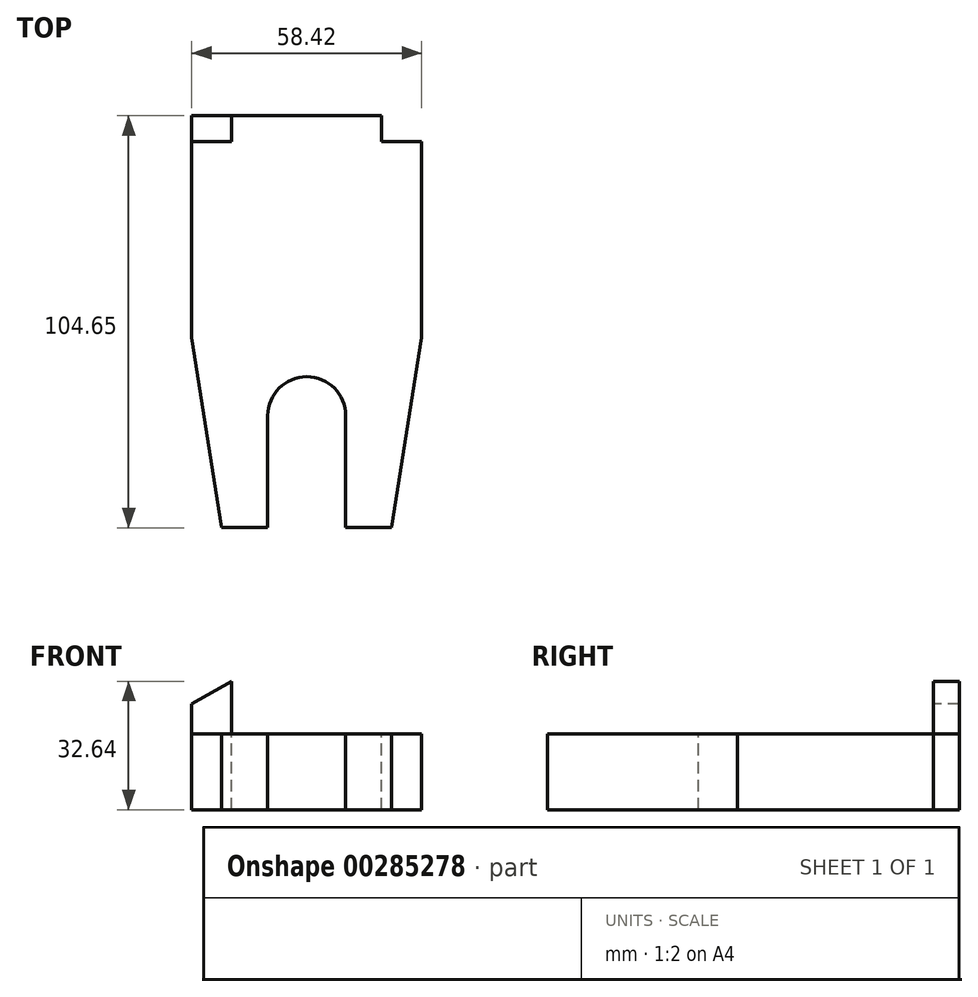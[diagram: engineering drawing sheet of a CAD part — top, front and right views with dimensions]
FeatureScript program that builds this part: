
annotation { "Feature Type Name" : "Feature", "Feature Type Description" : "" }
export const myFeature = defineFeature(function(context is Context, id is Id, definition is map)
    precondition{}
    {
        {
            var Q0;
            Q0=qCreatedBy(makeId("Front.planeOp"),FACE);
            var sketch = newSketch(context, id + "F0", { "sketchPlane" : qUnion([Q0])});
            skLineSegment(sketch, "E0.bottom", {"start": v(-54.99, -16.13) * mm, "end": v(3.43, -16.13) * mm});
            skLineSegment(sketch, "E0.top", {"start": v(-54.99, 3.18) * mm, "end": v(3.43, 3.18) * mm});
            skLineSegment(sketch, "E0.left", {"start": v(-54.99, -16.13) * mm, "end": v(-54.99, 3.18) * mm});
            skLineSegment(sketch, "E0.right", {"start": v(3.43, -16.13) * mm, "end": v(3.43, 3.18) * mm});
            skSolve(sketch);
        }
        {
            var Q0;
            Q0 = qSketchRegion(id + "F0", true);
            extrude(context, id + "F1", {"entities" : qUnion([Q0]), "depth" : 104.65 * mm});
        }
        {
            var Q0;
            Q0=makeQuery(id+"F1.opExtrude","SWEPT_FACE",FACE,{"disambiguationData":[OSD([sQuery(id+"F0.wireOp",EDGE,"E0.top")])]});
            var sketch = newSketch(context, id + "F2", { "sketchPlane" : qUnion([Q0])});
            skLineSegment(sketch, "E1", {"start": v(-25.78, -104.65) * mm, "end": v(-15.87, -104.65) * mm});
            skLineSegment(sketch, "E2", {"start": v(-25.78, -104.65) * mm, "end": v(-35.68, -104.65) * mm});
            skLineSegment(sketch, "E3", {"start": v(-15.87, -104.65) * mm, "end": v(-15.87, -76.2) * mm});
            skLineSegment(sketch, "E4", {"start": v(-15.87, -76.2) * mm, "end": v(-35.68, -76.2) * mm});
            skLineSegment(sketch, "E5", {"start": v(-35.68, -76.2) * mm, "end": v(-35.68, -104.65) * mm});
            skCircle(sketch, "E6", {"center": v(-25.78, -76.2) * mm, "radius": 9.9 * mm});
            skLineSegment(sketch, "E7", {"start": v(-54.99, -104.65) * mm, "end": v(-54.99, -56.39) * mm});
            skLineSegment(sketch, "E8", {"start": v(3.43, -104.65) * mm, "end": v(3.43, -56.39) * mm});
            skLineSegment(sketch, "E9", {"start": v(-54.99, -56.39) * mm, "end": v(-47.37, -104.65) * mm});
            skLineSegment(sketch, "E10", {"start": v(3.43, -56.39) * mm, "end": v(-4.19, -104.65) * mm});
            skLineSegment(sketch, "E11", {"start": v(-54.99, -104.65) * mm, "end": v(-47.37, -104.65) * mm});
            skLineSegment(sketch, "E12", {"start": v(3.43, -104.65) * mm, "end": v(-4.19, -104.65) * mm});
            skLineSegment(sketch, "E13", {"start": v(-54.99, 0) * mm, "end": v(-54.99, -23.88) * mm});
            skLineSegment(sketch, "E14", {"start": v(-54.99, -23.88) * mm, "end": v(3.43, -23.88) * mm});
            skLineSegment(sketch, "E15", {"start": v(3.43, -23.88) * mm, "end": v(3.43, 0) * mm});
            skLineSegment(sketch, "E16", {"start": v(3.43, 0) * mm, "end": v(-6.73, 0) * mm});
            skLineSegment(sketch, "E17", {"start": v(-54.99, 0) * mm, "end": v(-44.83, 0) * mm});
            skLineSegment(sketch, "E18", {"start": v(-44.83, 0) * mm, "end": v(-44.83, -6.6) * mm});
            skLineSegment(sketch, "E19", {"start": v(-6.73, 0) * mm, "end": v(-6.73, -6.6) * mm});
            skLineSegment(sketch, "E20", {"start": v(-44.83, -6.6) * mm, "end": v(-54.99, -6.6) * mm});
            skLineSegment(sketch, "E21", {"start": v(-54.99, -6.6) * mm, "end": v(-54.99, 0) * mm});
            skLineSegment(sketch, "E22", {"start": v(-6.73, -6.6) * mm, "end": v(3.43, -6.6) * mm});
            skSolve(sketch);
        }
        {
            var Q0;
            {var subQ0=sQuery(id+"F2.wireOp",EDGE,"E4");Q0=makeQuery(id+"F2.imprint","IMPRINT",FACE,{"disambiguationData":[TD([[makeQuery(id+"F2.imprint","IMPRINT",EDGE,{"derivedFrom":subQ0}),1.0]])]});}
            var Q1;
            {var subQ0=sQuery(id+"F2.wireOp",EDGE,"E4");Q1=makeQuery(id+"F2.imprint","IMPRINT",FACE,{"disambiguationData":[TD([[makeQuery(id+"F2.imprint","IMPRINT",EDGE,{"derivedFrom":subQ0}),-1.0]])]});}
            var Q2;
            Q2=makeQuery(id+"F2.imprint","IMPRINT",FACE,{"disambiguationData":[TD([[makeQuery(id+"F2.imprint","IMPRINT",EDGE,{"derivedFrom":sQuery(id+"F2.wireOp",EDGE,"E1")}),1.0]])]});
            var Q3;
            Q3=makeQuery(id+"F2.imprint","IMPRINT",FACE,{"disambiguationData":[TD([[makeQuery(id+"F2.imprint","IMPRINT",EDGE,{"derivedFrom":sQuery(id+"F2.wireOp",EDGE,"E7")}),-1.0]])]});
            var Q4;
            Q4=makeQuery(id+"F2.imprint","IMPRINT",FACE,{"disambiguationData":[TD([[makeQuery(id+"F2.imprint","IMPRINT",EDGE,{"derivedFrom":sQuery(id+"F2.wireOp",EDGE,"E8")}),1.0]])]});
            extrude(context, id + "F3", {"entities" : qUnion([Q0, Q1, Q2, Q3, Q4]), "operationType" : NewBodyOperationType.REMOVE, "oppositeDirection" : true, "depth" : 254 * mm});
        }
        {
            var Q0;
            Q0=makeQuery(id+"F2.imprint","IMPRINT",FACE,{"disambiguationData":[TD([[makeQuery(id+"F2.imprint","IMPRINT",EDGE,{"derivedFrom":sQuery(id+"F2.wireOp",EDGE,"E13")}),-1.0]])]});
            extrude(context, id + "F4", {"entities" : qUnion([Q0]), "operationType" : NewBodyOperationType.ADD, "depth" : 18.8 * mm});
        }
        {
            var Q0;
            Q0 = qSketchRegion(id + "F2", true);
            extrude(context, id + "F5", {"entities" : qUnion([Q0]), "operationType" : NewBodyOperationType.REMOVE, "oppositeDirection" : true, "depth" : 254 * mm});
        }
        {
            var Q0;
            Q0=makeQuery(id+"F4.opExtrude","SWEPT_FACE",FACE,{"disambiguationData":[OSD([sQuery(id+"F2.wireOp",EDGE,"E14")])]});
            var sketch = newSketch(context, id + "F6", { "sketchPlane" : qUnion([Q0])});
            skSolve(sketch);
        }
        {
            var Q0;
            {var subQ0=sQuery(id+"F0.wireOp",EDGE,"E0.top");Q0=makeQuery(id+"F4.boolean.opBoolean","MERGE",FACE,{"derivedFrom":[makeQuery(id+"F1.opExtrude","CAP_FACE",FACE,{"disambiguationData":[OSD([sQuery(id+"F0.wireOp",EDGE,"E0.bottom"),subQ0,sQuery(id+"F0.wireOp",EDGE,"E0.left"),sQuery(id+"F0.wireOp",EDGE,"E0.right")])],"isStart":true}),makeQuery(id+"F4.opExtrude","SWEPT_FACE",FACE,{"disambiguationData":[OSD([subQ0])]})]});}
            var sketch = newSketch(context, id + "F7", { "sketchPlane" : qUnion([Q0])});
            skLineSegment(sketch, "E23", {"start": v(35.14, 21.97) * mm, "end": v(86.7, -7.07) * mm});
            skLineSegment(sketch, "E24", {"start": v(86.7, -7.07) * mm, "end": v(86.7, 21.97) * mm});
            skLineSegment(sketch, "E25", {"start": v(86.7, 21.97) * mm, "end": v(35.14, 21.97) * mm});
            skSolve(sketch);
        }
        {
            var Q0;
            Q0 = qSketchRegion(id + "F7", true);
            extrude(context, id + "F8", {"entities" : qUnion([Q0]), "operationType" : NewBodyOperationType.REMOVE, "oppositeDirection" : true, "depth" : 25.4 * mm});
        }
        {
            var Q0;
            {var subQ0=sQuery(id+"F0.wireOp",EDGE,"E0.top");Q0=makeQuery(id+"F4.boolean.opBoolean","MERGE",FACE,{"derivedFrom":[makeQuery(id+"F1.opExtrude","CAP_FACE",FACE,{"disambiguationData":[OSD([sQuery(id+"F0.wireOp",EDGE,"E0.bottom"),subQ0,sQuery(id+"F0.wireOp",EDGE,"E0.left"),sQuery(id+"F0.wireOp",EDGE,"E0.right")])],"isStart":true}),makeQuery(id+"F4.opExtrude","SWEPT_FACE",FACE,{"disambiguationData":[OSD([subQ0])]})]});}
            var sketch = newSketch(context, id + "F9", { "sketchPlane" : qUnion([Q0])});
            skLineSegment(sketch, "E26", {"start": v(-3.44, 10.5) * mm, "end": v(34.18, 32.84) * mm});
            skLineSegment(sketch, "E27", {"start": v(34.18, 32.84) * mm, "end": v(-10.88, 32.84) * mm});
            skLineSegment(sketch, "E28", {"start": v(-10.88, 32.84) * mm, "end": v(-3.44, 10.5) * mm});
            skSolve(sketch);
        }
        {
            var Q0;
            Q0 = qSketchRegion(id + "F9", true);
            extrude(context, id + "F10", {"entities" : qUnion([Q0]), "operationType" : NewBodyOperationType.REMOVE, "oppositeDirection" : true, "depth" : 25.4 * mm});
        }
    });
